# Revit family: 304_36811e9d18dc4df997bc7bed7ffbaa
name_source: partatom
category: Pipe Accessories
revit_build: Autodesk Revit 2018 (Build: 20170223_1515(x64)
units: mm (PartAtom-declared; Revit-internal decimal feet)

## family parameters
Always vertical = Yes
Cut with Voids When Loaded = No
Part Type = Valve - Breaks Into
Round Connector Dimension = Use Diameter
Shared = No
Work Plane-Based = No

## types (3) — shared parameters
Description = 2-port valve PN10, adjustable Kvs and thermal actuator (on/off)
H10 = 52 mm
H11 = 13 mm  [stored 0.0426509 ft]
L10 = 22 mm
L11 = 24 mm
L12 = 26 mm
L2D = 39 mm
L2D_Min = 3048 mm  [stored 10 ft]
Manufacturer = Regin
QmdConnectorList = 301;D;302;D
R10 = 22 mm
R11 = 20 mm  [stored 0.0656168 ft]
R3 = 14 mm  [stored 0.0459318 ft]
R4 = 13 mm  [stored 0.0426509 ft]
W11 = 18 mm  [stored 0.0590551 ft]
W12 = 7 mm  [stored 0.0229659 ft]
W13 = 7 mm  [stored 0.0229659 ft]
W14 = 7 mm  [stored 0.0229659 ft]
W2D = 10 mm  [stored 0.0328084 ft]
magiPartTypeId = 304
magiProductFamilyId = 36811e9d18dc4df997bc7bed7ffbaa

## per-type parameters (varying)
| type | D | H | L1 | L2 | L_2 | R1 | R2 | magiProductId |
| CTV10+RTA(O)M100 (on/off) | 10 mm | 91 mm  [stored 0.298556 ft] | 8 mm  [stored 0.0262467 ft] | 2 mm  [stored 0.00656168 ft] | 19 mm  [stored 0.062336 ft] | 8 mm  [stored 0.0262467 ft] | 8 mm  [stored 0.0262467 ft] | 6115eb74b7fd45329ff878e4344b52 |
| CTV15-1,9+RTA(O)M100 (on/off) | 15 mm | 96 mm  [stored 0.314961 ft] | 8 mm  [stored 0.0262467 ft] | 3 mm  [stored 0.00984252 ft] | 22 mm | 11 mm | 12 mm  [stored 0.0393701 ft] | 509670f2f5f1411ea560bc581cec04 |
| CTV20+RTA(O)M100 (on/off) | 20 mm | 98 mm  [stored 0.321522 ft] | 10 mm  [stored 0.0328084 ft] | 3 mm  [stored 0.00984252 ft] | 24 mm | 15 mm  [stored 0.0492126 ft] | 17 mm | 714c3672adea4ae095e127d417439f |

note: column(s) folded — value = type name in every type: MC Product Code

note: [stored X ft] marks values corroborated as IEEE doubles in the binary element streams (Revit-internal decimal feet)

## geometry (parser evidence)
native form markers: Sweep x1
no freeform markers — native parametric forms only
